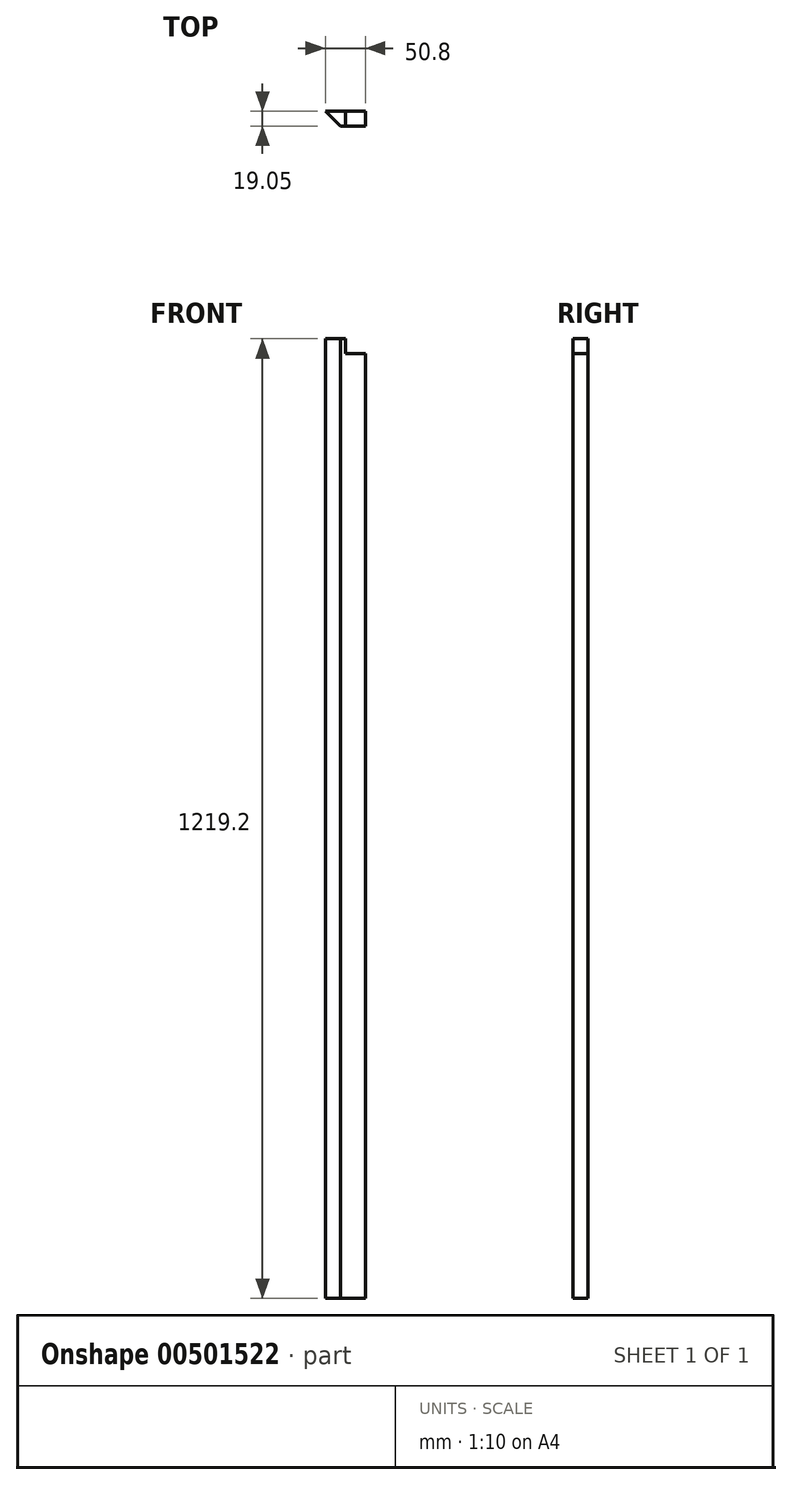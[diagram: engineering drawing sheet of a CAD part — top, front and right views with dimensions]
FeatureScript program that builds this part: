
annotation { "Feature Type Name" : "Feature", "Feature Type Description" : "" }
export const myFeature = defineFeature(function(context is Context, id is Id, definition is map)
    precondition{}
    {
        {
            var Q0;
            Q0=qCreatedBy(makeId("Top.planeOp"),FACE);
            var sketch = newSketch(context, id + "F0", { "sketchPlane" : qUnion([Q0])});
            skLineSegment(sketch, "E0", {"start": v(0, 0) * mm, "end": v(0, 19.05) * mm});
            skLineSegment(sketch, "E1", {"start": v(0, 19.05) * mm, "end": v(-50.8, 19.05) * mm});
            skLineSegment(sketch, "E2", {"start": v(-50.8, 19.05) * mm, "end": v(-31.75, 0) * mm});
            skLineSegment(sketch, "E3", {"start": v(-31.75, 0) * mm, "end": v(0, 0) * mm});
            skSolve(sketch);
        }
        {
            var Q0;
            Q0=makeQuery(id+"F0.imprint","IMPRINT",FACE,{"disambiguationData":[TD([[makeQuery(id+"F0.imprint","IMPRINT",EDGE,{"derivedFrom":sQuery(id+"F0.wireOp",EDGE,"E0")}),1.0]])]});
            extrude(context, id + "F1", {"entities" : qUnion([Q0]), "oppositeDirection" : true, "depth" : 1219.2 * mm});
        }
        {
            var Q0;
            Q0=makeQuery(id+"F1.opExtrude","SWEPT_FACE",FACE,{"disambiguationData":[OSD([sQuery(id+"F0.wireOp",EDGE,"E1")])]});
            var sketch = newSketch(context, id + "F2", { "sketchPlane" : qUnion([Q0])});
            skLineSegment(sketch, "E4.bottom", {"start": v(0, 0) * mm, "end": v(25.4, 0) * mm});
            skLineSegment(sketch, "E4.top", {"start": v(0, -19.05) * mm, "end": v(25.4, -19.05) * mm});
            skLineSegment(sketch, "E4.left", {"start": v(0, 0) * mm, "end": v(0, -19.05) * mm});
            skLineSegment(sketch, "E4.right", {"start": v(25.4, 0) * mm, "end": v(25.4, -19.05) * mm});
            skSolve(sketch);
        }
        {
            var Q0;
            Q0=makeQuery(id+"F2.imprint","IMPRINT",FACE,{"disambiguationData":[TD([[makeQuery(id+"F2.imprint","IMPRINT",EDGE,{"derivedFrom":sQuery(id+"F2.wireOp",EDGE,"E4.bottom")}),-1.0]])]});
            extrude(context, id + "F3", {"entities" : qUnion([Q0]), "operationType" : NewBodyOperationType.REMOVE, "endBound" : BoundingType.THROUGH_ALL, "oppositeDirection" : true, "depth" : 25.4 * mm});
        }
    });
